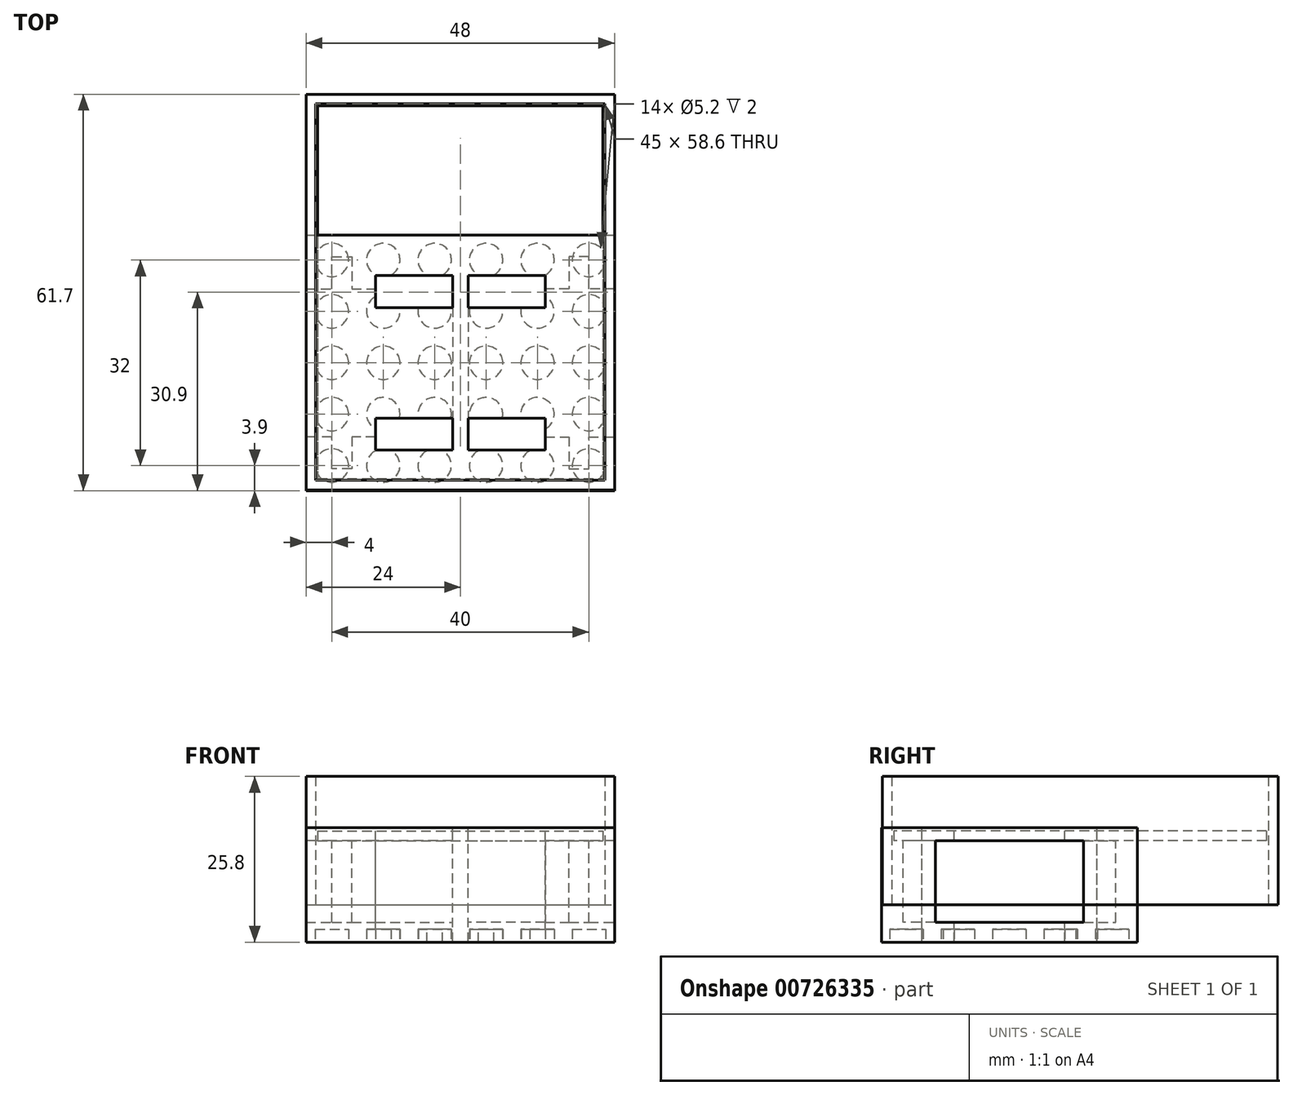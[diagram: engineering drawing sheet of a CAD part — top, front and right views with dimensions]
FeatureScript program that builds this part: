
annotation { "Feature Type Name" : "Feature", "Feature Type Description" : "" }
export const myFeature = defineFeature(function(context is Context, id is Id, definition is map)
    precondition{}
    {
        {
            var Q0;
            Q0=qCreatedBy(makeId("Top.planeOp"),FACE);
            var sketch = newSketch(context, id + "F0", { "sketchPlane" : qUnion([Q0])});
            skLineSegment(sketch, "E0.bottom", {"start": v(-24, 20) * mm, "end": v(24, 20) * mm});
            skLineSegment(sketch, "E0.top", {"start": v(-24, -20) * mm, "end": v(24, -20) * mm});
            skLineSegment(sketch, "E0.left", {"start": v(-24, 20) * mm, "end": v(-24, -20) * mm});
            skLineSegment(sketch, "E0.right", {"start": v(24, 20) * mm, "end": v(24, -20) * mm});
            skSolve(sketch);
        }
        {
            var Q0;
            Q0=makeQuery(id+"F0.imprint","IMPRINT",FACE,{"disambiguationData":[TD([[makeQuery(id+"F0.imprint","IMPRINT",EDGE,{"derivedFrom":sQuery(id+"F0.wireOp",EDGE,"E0.bottom")}),-1.0]])]});
            extrude(context, id + "F1", {"entities" : qUnion([Q0]), "depth" : 2 * mm, "offsetDistance" : 25 * mm});
        }
        {
            var Q0;
            Q0=qCreatedBy(makeId("Top.planeOp"),FACE);
            var sketch = newSketch(context, id + "F2", { "sketchPlane" : qUnion([Q0])});
            skLineSegment(sketch, "E1.bottom", {"start": v(24, -11.23) * mm, "end": v(19.7, -11.23) * mm});
            skLineSegment(sketch, "E1.top", {"start": v(24, 11.23) * mm, "end": v(19.7, 11.23) * mm});
            skLineSegment(sketch, "E1.left", {"start": v(24, -11.23) * mm, "end": v(24, 11.23) * mm});
            skLineSegment(sketch, "E1.right", {"start": v(1.5, -11.23) * mm, "end": v(1.5, 11.23) * mm});
            skLineSegment(sketch, "E2", {"start": v(19.7, -11.23) * mm, "end": v(19.7, -16.23) * mm});
            skLineSegment(sketch, "E3", {"start": v(19.7, -16.23) * mm, "end": v(17.2, -16.23) * mm});
            skLineSegment(sketch, "E4", {"start": v(17.2, -16.23) * mm, "end": v(17.2, -11.23) * mm});
            skLineSegment(sketch, "E5", {"start": v(19.7, 11.23) * mm, "end": v(19.7, 16.23) * mm});
            skLineSegment(sketch, "E6", {"start": v(19.7, 16.23) * mm, "end": v(17.2, 16.23) * mm});
            skLineSegment(sketch, "E7", {"start": v(17.2, 16.23) * mm, "end": v(17.2, 11.23) * mm});
            skLineSegment(sketch, "E8.trimOffspring", {"start": v(17.2, -11.23) * mm, "end": v(1.5, -11.23) * mm});
            skLineSegment(sketch, "E9.trimOffspring", {"start": v(17.2, 11.23) * mm, "end": v(1.5, 11.23) * mm});
            skLineSegment(sketch, "E10.MirrorCS", {"start": v(-24, -11.23) * mm, "end": v(-19.7, -11.23) * mm});
            skLineSegment(sketch, "E11.MirrorCS", {"start": v(-24, 11.23) * mm, "end": v(-19.7, 11.23) * mm});
            skLineSegment(sketch, "E12.MirrorCS", {"start": v(-24, -11.23) * mm, "end": v(-24, 11.23) * mm});
            skLineSegment(sketch, "E13.MirrorCS", {"start": v(-1.5, -11.23) * mm, "end": v(-1.5, 11.23) * mm});
            skLineSegment(sketch, "E14.MirrorCS", {"start": v(-19.7, -11.23) * mm, "end": v(-19.7, -16.23) * mm});
            skLineSegment(sketch, "E15.MirrorCS", {"start": v(-19.7, 16.23) * mm, "end": v(-17.2, 16.23) * mm});
            skLineSegment(sketch, "E16.MirrorCS", {"start": v(-19.7, -16.23) * mm, "end": v(-17.2, -16.23) * mm});
            skLineSegment(sketch, "E17.MirrorCS", {"start": v(-19.7, 11.23) * mm, "end": v(-19.7, 16.23) * mm});
            skLineSegment(sketch, "E18.MirrorCS", {"start": v(-17.2, -16.23) * mm, "end": v(-17.2, -11.23) * mm});
            skLineSegment(sketch, "E19.MirrorCS", {"start": v(-17.2, -11.23) * mm, "end": v(-1.5, -11.23) * mm});
            skLineSegment(sketch, "E20.MirrorCS", {"start": v(-17.2, 16.23) * mm, "end": v(-17.2, 11.23) * mm});
            skLineSegment(sketch, "E21.MirrorCS", {"start": v(-17.2, 11.23) * mm, "end": v(-1.5, 11.23) * mm});
            skSolve(sketch);
        }
        {
            var Q0;
            Q0=makeQuery(id+"F1.opExtrude","CAP_FACE",FACE,{"disambiguationData":[OSD([sQuery(id+"F0.wireOp",EDGE,"E0.bottom"),sQuery(id+"F0.wireOp",EDGE,"E0.top"),sQuery(id+"F0.wireOp",EDGE,"E0.left"),sQuery(id+"F0.wireOp",EDGE,"E0.right")])],"isStart":true});
            var sketch = newSketch(context, id + "F3", { "sketchPlane" : qUnion([Q0])});
            skLineSegment(sketch, "E22.bottom", {"start": v(24, -27.9) * mm, "end": v(-1, -27.9) * mm});
            skLineSegment(sketch, "E22.top", {"start": v(24, 27.9) * mm, "end": v(-1, 27.9) * mm});
            skLineSegment(sketch, "E22.left", {"start": v(24, -27.9) * mm, "end": v(24, -11.53) * mm});
            skLineSegment(sketch, "E22.right", {"start": v(-1, -27.9) * mm, "end": v(-1, 27.9) * mm});
            skLineSegment(sketch, "E23", {"start": v(24, -11.53) * mm, "end": v(20, -11.53) * mm});
            skLineSegment(sketch, "E24", {"start": v(20, -11.53) * mm, "end": v(20, -16.53) * mm});
            skLineSegment(sketch, "E25", {"start": v(20, -16.53) * mm, "end": v(16.9, -16.53) * mm});
            skLineSegment(sketch, "E26", {"start": v(16.9, -16.53) * mm, "end": v(16.9, -11.53) * mm});
            skLineSegment(sketch, "E27", {"start": v(16.9, -11.53) * mm, "end": v(1.2, -11.53) * mm});
            skLineSegment(sketch, "E28", {"start": v(1.2, -11.53) * mm, "end": v(1.2, 11.53) * mm});
            skLineSegment(sketch, "E29", {"start": v(1.2, 11.53) * mm, "end": v(16.9, 11.53) * mm});
            skLineSegment(sketch, "E30", {"start": v(16.9, 11.53) * mm, "end": v(16.9, 16.53) * mm});
            skLineSegment(sketch, "E31", {"start": v(16.9, 16.53) * mm, "end": v(20, 16.53) * mm});
            skLineSegment(sketch, "E32", {"start": v(20, 16.53) * mm, "end": v(20, 11.53) * mm});
            skLineSegment(sketch, "E33", {"start": v(20, 11.53) * mm, "end": v(24, 11.53) * mm});
            skLineSegment(sketch, "E34.trimOffspring", {"start": v(24, 11.53) * mm, "end": v(24, 27.9) * mm});
            skLineSegment(sketch, "E35.MirrorCS", {"start": v(-16.9, 16.53) * mm, "end": v(-20, 16.53) * mm});
            skLineSegment(sketch, "E36.MirrorCS", {"start": v(-16.9, 11.53) * mm, "end": v(-16.9, 16.53) * mm});
            skLineSegment(sketch, "E37.MirrorCS", {"start": v(-1.2, 11.53) * mm, "end": v(-16.9, 11.53) * mm});
            skLineSegment(sketch, "E38.MirrorCS", {"start": v(-1.2, -11.53) * mm, "end": v(-1.2, 11.53) * mm});
            skLineSegment(sketch, "E39.MirrorCS", {"start": v(-16.9, -11.53) * mm, "end": v(-1.2, -11.53) * mm});
            skLineSegment(sketch, "E40.MirrorCS", {"start": v(-16.9, -16.53) * mm, "end": v(-16.9, -11.53) * mm});
            skLineSegment(sketch, "E41.MirrorCS", {"start": v(-20, -16.53) * mm, "end": v(-16.9, -16.53) * mm});
            skLineSegment(sketch, "E42.MirrorCS", {"start": v(-20, -11.53) * mm, "end": v(-20, -16.53) * mm});
            skLineSegment(sketch, "E43.MirrorCS", {"start": v(-24, -11.53) * mm, "end": v(-20, -11.53) * mm});
            skLineSegment(sketch, "E44.MirrorCS", {"start": v(1, -27.9) * mm, "end": v(1, 27.9) * mm});
            skLineSegment(sketch, "E45.MirrorCS", {"start": v(-24, -27.9) * mm, "end": v(-24, -11.53) * mm});
            skLineSegment(sketch, "E46.MirrorCS", {"start": v(-24, 27.9) * mm, "end": v(1, 27.9) * mm});
            skLineSegment(sketch, "E47.MirrorCS", {"start": v(-24, -27.9) * mm, "end": v(1, -27.9) * mm});
            skLineSegment(sketch, "E48.MirrorCS", {"start": v(-24, 11.53) * mm, "end": v(-24, 27.9) * mm});
            skLineSegment(sketch, "E49.MirrorCS", {"start": v(-20, 16.53) * mm, "end": v(-20, 11.53) * mm});
            skLineSegment(sketch, "E50.MirrorCS", {"start": v(-20, 11.53) * mm, "end": v(-24, 11.53) * mm});
            skSolve(sketch);
        }
        {
            var Q0;
            Q0 = qSketchRegion(id + "F3", true);
            extrude(context, id + "F4", {"entities" : qUnion([Q0]), "depth" : 12.7 * mm, "offsetDistance" : 25 * mm});
        }
        {
            var Q0;
            Q0=makeQuery(id+"F4.opExtrude","CAP_FACE",FACE,{"disambiguationData":[OSD([sQuery(id+"F3.wireOp",EDGE,"E22.bottom"),sQuery(id+"F3.wireOp",EDGE,"E22.top"),sQuery(id+"F3.wireOp",EDGE,"E22.left"),sQuery(id+"F3.wireOp",EDGE,"E22.right"),sQuery(id+"F3.wireOp",EDGE,"E23"),sQuery(id+"F3.wireOp",EDGE,"E24"),sQuery(id+"F3.wireOp",EDGE,"E25"),sQuery(id+"F3.wireOp",EDGE,"E26"),sQuery(id+"F3.wireOp",EDGE,"E27"),sQuery(id+"F3.wireOp",EDGE,"E28"),sQuery(id+"F3.wireOp",EDGE,"E29"),sQuery(id+"F3.wireOp",EDGE,"E30"),sQuery(id+"F3.wireOp",EDGE,"E31"),sQuery(id+"F3.wireOp",EDGE,"E32"),sQuery(id+"F3.wireOp",EDGE,"E33"),sQuery(id+"F3.wireOp",EDGE,"E34.trimOffspring")])],"isStart":false});
            var sketch = newSketch(context, id + "F5", { "sketchPlane" : qUnion([Q0])});
            skLineSegment(sketch, "E51.bottom", {"start": v(24, -27.9) * mm, "end": v(-24, -27.9) * mm});
            skLineSegment(sketch, "E51.top", {"start": v(24, 27.9) * mm, "end": v(-24, 27.9) * mm});
            skLineSegment(sketch, "E51.left", {"start": v(24, -27.9) * mm, "end": v(24, 27.9) * mm});
            skLineSegment(sketch, "E51.right", {"start": v(-24, -27.9) * mm, "end": v(-24, 27.9) * mm});
            skSolve(sketch);
        }
        {
            var Q0;
            Q0 = qSketchRegion(id + "F5", true);
            extrude(context, id + "F6", {"entities" : qUnion([Q0]), "operationType" : NewBodyOperationType.ADD, "depth" : 3.1 * mm, "offsetDistance" : 25 * mm});
        }
        {
            var Q0;
            Q0=makeQuery(id+"F4.opExtrude","CAP_FACE",FACE,{"disambiguationData":[OSD([sQuery(id+"F3.wireOp",EDGE,"E22.bottom"),sQuery(id+"F3.wireOp",EDGE,"E22.top"),sQuery(id+"F3.wireOp",EDGE,"E22.left"),sQuery(id+"F3.wireOp",EDGE,"E22.right"),sQuery(id+"F3.wireOp",EDGE,"E23"),sQuery(id+"F3.wireOp",EDGE,"E24"),sQuery(id+"F3.wireOp",EDGE,"E25"),sQuery(id+"F3.wireOp",EDGE,"E26"),sQuery(id+"F3.wireOp",EDGE,"E27"),sQuery(id+"F3.wireOp",EDGE,"E28"),sQuery(id+"F3.wireOp",EDGE,"E29"),sQuery(id+"F3.wireOp",EDGE,"E30"),sQuery(id+"F3.wireOp",EDGE,"E31"),sQuery(id+"F3.wireOp",EDGE,"E32"),sQuery(id+"F3.wireOp",EDGE,"E33"),sQuery(id+"F3.wireOp",EDGE,"E34.trimOffspring")])],"isStart":true});
            var sketch = newSketch(context, id + "F7", { "sketchPlane" : qUnion([Q0])});
            skLineSegment(sketch, "E52", {"start": v(42.9, 0) * mm, "end": v(-13.7, 0) * mm, "construction": true});
            skCircle(sketch, "E53", {"center": v(4, -16) * mm, "radius": 2.4 * mm});
            skCircle(sketch, "E54", {"center": v(12, -16) * mm, "radius": 2.4 * mm});
            skCircle(sketch, "E55", {"center": v(4, -24) * mm, "radius": 2.4 * mm});
            skCircle(sketch, "E56", {"center": v(12, -24) * mm, "radius": 2.4 * mm});
            skCircle(sketch, "E57", {"center": v(20, -24) * mm, "radius": 2.4 * mm});
            skCircle(sketch, "E58.MirrorC", {"center": v(20, 24) * mm, "radius": 2.4 * mm});
            skCircle(sketch, "E59.MirrorC", {"center": v(12, 16) * mm, "radius": 2.4 * mm});
            skCircle(sketch, "E60.MirrorC", {"center": v(4, 16) * mm, "radius": 2.4 * mm});
            skCircle(sketch, "E61.MirrorC", {"center": v(12, 24) * mm, "radius": 2.4 * mm});
            skCircle(sketch, "E62.MirrorC", {"center": v(4, 24) * mm, "radius": 2.4 * mm});
            skCircle(sketch, "E63.MirrorC", {"center": v(-20, -24) * mm, "radius": 2.4 * mm});
            skCircle(sketch, "E64.MirrorC", {"center": v(-4, 16) * mm, "radius": 2.4 * mm});
            skCircle(sketch, "E65.MirrorC", {"center": v(-12, 16) * mm, "radius": 2.4 * mm});
            skCircle(sketch, "E66.MirrorC", {"center": v(-12, -24) * mm, "radius": 2.4 * mm});
            skCircle(sketch, "E67.MirrorC", {"center": v(-4, -16) * mm, "radius": 2.4 * mm});
            skCircle(sketch, "E68.MirrorC", {"center": v(-4, -24) * mm, "radius": 2.4 * mm});
            skCircle(sketch, "E69.MirrorC", {"center": v(-12, -16) * mm, "radius": 2.4 * mm});
            skCircle(sketch, "E70.MirrorC", {"center": v(-20, 24) * mm, "radius": 2.4 * mm});
            skCircle(sketch, "E71.MirrorC", {"center": v(-4, 24) * mm, "radius": 2.4 * mm});
            skCircle(sketch, "E72.MirrorC", {"center": v(-12, 24) * mm, "radius": 2.4 * mm});
            skSolve(sketch);
        }
        {
            var Q0;
            Q0 = qSketchRegion(id + "F7", true);
            extrude(context, id + "F8", {"entities" : qUnion([Q0]), "operationType" : NewBodyOperationType.ADD, "depth" : 1.6 * mm, "offsetDistance" : 25 * mm});
        }
        {
            var Q0;
            {var subQ0=sQuery(id+"F5.wireOp",EDGE,"E51.left");Q0=makeQuery(id+"F6.boolean.opBoolean","SPLIT",FACE,{"disambiguationData":[TD([makeQuery(id+"F4.opExtrude","SWEPT_FACE",FACE,{"disambiguationData":[OSD([sQuery(id+"F3.wireOp",EDGE,"E22.left")])]})])],"derivedFrom":makeQuery(id+"F6.opExtrude","CAP_FACE",FACE,{"disambiguationData":[OSD([sQuery(id+"F5.wireOp",EDGE,"E51.bottom"),sQuery(id+"F5.wireOp",EDGE,"E51.top"),subQ0,sQuery(id+"F5.wireOp",EDGE,"E51.right")])],"isStart":true})});}
            var sketch = newSketch(context, id + "F9", { "sketchPlane" : qUnion([Q0])});
            skLineSegment(sketch, "E73.bottom", {"start": v(1.2, -8.6) * mm, "end": v(13.2, -8.6) * mm});
            skLineSegment(sketch, "E73.top", {"start": v(1.2, -13.6) * mm, "end": v(13.2, -13.6) * mm});
            skLineSegment(sketch, "E73.left", {"start": v(1.2, -8.6) * mm, "end": v(1.2, -13.6) * mm});
            skLineSegment(sketch, "E73.right", {"start": v(13.2, -8.6) * mm, "end": v(13.2, -13.6) * mm});
            skLineSegment(sketch, "E74.MirrorCS", {"start": v(-1.2, -8.6) * mm, "end": v(-13.2, -8.6) * mm});
            skLineSegment(sketch, "E75.MirrorCS", {"start": v(-13.2, -8.6) * mm, "end": v(-13.2, -13.6) * mm});
            skLineSegment(sketch, "E76.MirrorCS", {"start": v(-1.2, -8.6) * mm, "end": v(-1.2, -13.6) * mm});
            skLineSegment(sketch, "E77.MirrorCS", {"start": v(-1.2, -13.6) * mm, "end": v(-13.2, -13.6) * mm});
            skLineSegment(sketch, "E78.MirrorCS", {"start": v(-1.2, 8.6) * mm, "end": v(-1.2, 13.6) * mm});
            skLineSegment(sketch, "E79.MirrorCS", {"start": v(1.2, 8.6) * mm, "end": v(13.2, 8.6) * mm});
            skLineSegment(sketch, "E80.MirrorCS", {"start": v(13.2, 8.6) * mm, "end": v(13.2, 13.6) * mm});
            skLineSegment(sketch, "E81.MirrorCS", {"start": v(-1.2, 13.6) * mm, "end": v(-13.2, 13.6) * mm});
            skLineSegment(sketch, "E82.MirrorCS", {"start": v(-13.2, 8.6) * mm, "end": v(-13.2, 13.6) * mm});
            skLineSegment(sketch, "E83.MirrorCS", {"start": v(-1.2, 8.6) * mm, "end": v(-13.2, 8.6) * mm});
            skLineSegment(sketch, "E84.MirrorCS", {"start": v(1.2, 8.6) * mm, "end": v(1.2, 13.6) * mm});
            skLineSegment(sketch, "E85.MirrorCS", {"start": v(1.2, 13.6) * mm, "end": v(13.2, 13.6) * mm});
            skSolve(sketch);
        }
        {
            var Q0;
            Q0 = qSketchRegion(id + "F9", true);
            extrude(context, id + "F10", {"entities" : qUnion([Q0]), "operationType" : NewBodyOperationType.REMOVE, "endBound" : BoundingType.SYMMETRIC, "oppositeDirection" : true, "depth" : 50 * mm, "offsetDistance" : 25 * mm});
        }
        {
            var Q0;
            Q0=makeQuery(id+"F4.opExtrude","CAP_FACE",FACE,{"disambiguationData":[OSD([sQuery(id+"F3.wireOp",EDGE,"E22.bottom"),sQuery(id+"F3.wireOp",EDGE,"E22.top"),sQuery(id+"F3.wireOp",EDGE,"E22.left"),sQuery(id+"F3.wireOp",EDGE,"E23"),sQuery(id+"F3.wireOp",EDGE,"E24"),sQuery(id+"F3.wireOp",EDGE,"E25"),sQuery(id+"F3.wireOp",EDGE,"E26"),sQuery(id+"F3.wireOp",EDGE,"E27"),sQuery(id+"F3.wireOp",EDGE,"E28"),sQuery(id+"F3.wireOp",EDGE,"E29"),sQuery(id+"F3.wireOp",EDGE,"E30"),sQuery(id+"F3.wireOp",EDGE,"E31"),sQuery(id+"F3.wireOp",EDGE,"E32"),sQuery(id+"F3.wireOp",EDGE,"E33"),sQuery(id+"F3.wireOp",EDGE,"E34.trimOffspring"),sQuery(id+"F3.wireOp",EDGE,"E35.MirrorCS"),sQuery(id+"F3.wireOp",EDGE,"E36.MirrorCS"),sQuery(id+"F3.wireOp",EDGE,"E37.MirrorCS"),sQuery(id+"F3.wireOp",EDGE,"E38.MirrorCS"),sQuery(id+"F3.wireOp",EDGE,"E39.MirrorCS"),sQuery(id+"F3.wireOp",EDGE,"E40.MirrorCS"),sQuery(id+"F3.wireOp",EDGE,"E41.MirrorCS"),sQuery(id+"F3.wireOp",EDGE,"E42.MirrorCS"),sQuery(id+"F3.wireOp",EDGE,"E43.MirrorCS"),sQuery(id+"F3.wireOp",EDGE,"E45.MirrorCS"),sQuery(id+"F3.wireOp",EDGE,"E46.MirrorCS"),sQuery(id+"F3.wireOp",EDGE,"E47.MirrorCS"),sQuery(id+"F3.wireOp",EDGE,"E48.MirrorCS"),sQuery(id+"F3.wireOp",EDGE,"E49.MirrorCS"),sQuery(id+"F3.wireOp",EDGE,"E50.MirrorCS")])],"isStart":true});
            var sketch = newSketch(context, id + "F11", { "sketchPlane" : qUnion([Q0])});
            skLineSegment(sketch, "E86.bottom", {"start": v(-32.74, 19.9) * mm, "end": v(43.37, 19.9) * mm});
            skLineSegment(sketch, "E86.top", {"start": v(-32.74, 44.05) * mm, "end": v(43.37, 44.05) * mm});
            skLineSegment(sketch, "E86.left", {"start": v(-32.74, 19.9) * mm, "end": v(-32.74, 44.05) * mm});
            skLineSegment(sketch, "E86.right", {"start": v(43.37, 19.9) * mm, "end": v(43.37, 44.05) * mm});
            skLineSegment(sketch, "E87.bottom", {"start": v(-31.38, -34.8) * mm, "end": v(34.1, -34.8) * mm});
            skLineSegment(sketch, "E87.top", {"start": v(-31.38, -19.9) * mm, "end": v(34.1, -19.9) * mm});
            skLineSegment(sketch, "E87.left", {"start": v(-31.38, -34.8) * mm, "end": v(-31.38, -19.9) * mm});
            skLineSegment(sketch, "E87.right", {"start": v(34.1, -34.8) * mm, "end": v(34.1, -19.9) * mm});
            skSolve(sketch);
        }
        {
            var Q0;
            Q0 = qSketchRegion(id + "F11", true);
            extrude(context, id + "F12", {"entities" : qUnion([Q0]), "operationType" : NewBodyOperationType.REMOVE, "endBound" : BoundingType.SYMMETRIC, "oppositeDirection" : true, "depth" : 50 * mm, "offsetDistance" : 25 * mm});
        }
        {
            var Q0;
            Q0=makeQuery(id+"F6.opExtrude","CAP_FACE",FACE,{"disambiguationData":[OSD([sQuery(id+"F5.wireOp",EDGE,"E51.bottom"),sQuery(id+"F5.wireOp",EDGE,"E51.top"),sQuery(id+"F5.wireOp",EDGE,"E51.left"),sQuery(id+"F5.wireOp",EDGE,"E51.right")])],"isStart":false});
            var sketch = newSketch(context, id + "F13", { "sketchPlane" : qUnion([Q0])});
            skCircle(sketch, "E88", {"center": v(4, 8) * mm, "radius": 2.6 * mm});
            skCircle(sketch, "E89", {"center": v(12, 8) * mm, "radius": 2.6 * mm});
            skCircle(sketch, "E90", {"center": v(20, 8) * mm, "radius": 2.6 * mm});
            skCircle(sketch, "E91", {"center": v(20, 16) * mm, "radius": 2.6 * mm});
            skCircle(sketch, "E92", {"center": v(12, 16) * mm, "radius": 2.6 * mm});
            skCircle(sketch, "E93", {"center": v(4, 16) * mm, "radius": 2.6 * mm});
            skCircle(sketch, "E94.MirrorC", {"center": v(4, -8) * mm, "radius": 2.6 * mm});
            skCircle(sketch, "E95.MirrorC", {"center": v(12, -8) * mm, "radius": 2.6 * mm});
            skCircle(sketch, "E96.MirrorC", {"center": v(12, -16) * mm, "radius": 2.6 * mm});
            skCircle(sketch, "E97.MirrorC", {"center": v(4, -16) * mm, "radius": 2.6 * mm});
            skCircle(sketch, "E98.MirrorC", {"center": v(20, -8) * mm, "radius": 2.6 * mm});
            skCircle(sketch, "E99.MirrorC", {"center": v(20, -16) * mm, "radius": 2.6 * mm});
            skCircle(sketch, "E100", {"center": v(20, 0) * mm, "radius": 2.6 * mm});
            skCircle(sketch, "E101", {"center": v(12, 0) * mm, "radius": 2.6 * mm});
            skCircle(sketch, "E102", {"center": v(4, 0) * mm, "radius": 2.6 * mm});
            skCircle(sketch, "E103.MirrorC", {"center": v(-12, 8) * mm, "radius": 2.6 * mm});
            skCircle(sketch, "E104.MirrorC", {"center": v(-20, 8) * mm, "radius": 2.6 * mm});
            skCircle(sketch, "E105.MirrorC", {"center": v(-4, 8) * mm, "radius": 2.6 * mm});
            skCircle(sketch, "E106.MirrorC", {"center": v(-20, 0) * mm, "radius": 2.6 * mm});
            skCircle(sketch, "E107.MirrorC", {"center": v(-20, -8) * mm, "radius": 2.6 * mm});
            skCircle(sketch, "E108.MirrorC", {"center": v(-4, -16) * mm, "radius": 2.6 * mm});
            skCircle(sketch, "E109.MirrorC", {"center": v(-12, -16) * mm, "radius": 2.6 * mm});
            skCircle(sketch, "E110.MirrorC", {"center": v(-4, 0) * mm, "radius": 2.6 * mm});
            skCircle(sketch, "E111.MirrorC", {"center": v(-12, -8) * mm, "radius": 2.6 * mm});
            skCircle(sketch, "E112.MirrorC", {"center": v(-12, 0) * mm, "radius": 2.6 * mm});
            skCircle(sketch, "E113.MirrorC", {"center": v(-20, 16) * mm, "radius": 2.6 * mm});
            skCircle(sketch, "E114.MirrorC", {"center": v(-20, -16) * mm, "radius": 2.6 * mm});
            skCircle(sketch, "E115.MirrorC", {"center": v(-4, -8) * mm, "radius": 2.6 * mm});
            skCircle(sketch, "E116.MirrorC", {"center": v(-4, 16) * mm, "radius": 2.6 * mm});
            skCircle(sketch, "E117.MirrorC", {"center": v(-12, 16) * mm, "radius": 2.6 * mm});
            skSolve(sketch);
        }
        {
            var Q0;
            Q0 = qSketchRegion(id + "F13", true);
            extrude(context, id + "F14", {"entities" : qUnion([Q0]), "operationType" : NewBodyOperationType.REMOVE, "oppositeDirection" : true, "depth" : 2 * mm, "offsetDistance" : 25 * mm});
        }
        {
            var Q0;
            Q0=makeQuery(id+"F6.opExtrude","CAP_FACE",FACE,{"disambiguationData":[OSD([sQuery(id+"F5.wireOp",EDGE,"E51.bottom"),sQuery(id+"F5.wireOp",EDGE,"E51.top"),sQuery(id+"F5.wireOp",EDGE,"E51.left"),sQuery(id+"F5.wireOp",EDGE,"E51.right")])],"isStart":false});
            var sketch = newSketch(context, id + "F15", { "sketchPlane" : qUnion([Q0])});
            skLineSegment(sketch, "E118.bottom", {"start": v(13.2, 12.62) * mm, "end": v(10.8, 12.62) * mm});
            skLineSegment(sketch, "E118.top", {"start": v(13.2, 15.52) * mm, "end": v(10.8, 15.52) * mm});
            skLineSegment(sketch, "E118.left", {"start": v(13.2, 12.62) * mm, "end": v(13.2, 15.52) * mm});
            skLineSegment(sketch, "E118.right", {"start": v(10.8, 12.62) * mm, "end": v(10.8, 15.52) * mm});
            skLineSegment(sketch, "E119", {"start": v(12, 16) * mm, "end": v(12, 11.4) * mm, "construction": true});
            skLineSegment(sketch, "E120", {"start": v(4, 16) * mm, "end": v(4, 11.42) * mm, "construction": true});
            skLineSegment(sketch, "E121.bottom", {"start": v(5.2, 15.52) * mm, "end": v(2.8, 15.52) * mm});
            skLineSegment(sketch, "E121.top", {"start": v(5.2, 12.4) * mm, "end": v(2.8, 12.4) * mm});
            skLineSegment(sketch, "E121.left", {"start": v(5.2, 15.52) * mm, "end": v(5.2, 12.4) * mm});
            skLineSegment(sketch, "E121.right", {"start": v(2.8, 15.52) * mm, "end": v(2.8, 12.4) * mm});
            skLineSegment(sketch, "E122.MirrorCS", {"start": v(5.2, -15.52) * mm, "end": v(2.8, -15.52) * mm});
            skLineSegment(sketch, "E123.MirrorCS", {"start": v(13.2, -12.62) * mm, "end": v(10.8, -12.62) * mm});
            skLineSegment(sketch, "E124.MirrorCS", {"start": v(13.2, -15.52) * mm, "end": v(10.8, -15.52) * mm});
            skLineSegment(sketch, "E125.MirrorCS", {"start": v(13.2, -12.62) * mm, "end": v(13.2, -15.52) * mm});
            skLineSegment(sketch, "E126.MirrorCS", {"start": v(10.8, -12.62) * mm, "end": v(10.8, -15.52) * mm});
            skLineSegment(sketch, "E127.MirrorCS", {"start": v(5.2, -12.4) * mm, "end": v(2.8, -12.4) * mm});
            skLineSegment(sketch, "E128.MirrorCS", {"start": v(2.8, -15.52) * mm, "end": v(2.8, -12.4) * mm});
            skLineSegment(sketch, "E129.MirrorCS", {"start": v(5.2, -15.52) * mm, "end": v(5.2, -12.4) * mm});
            skLineSegment(sketch, "E130.MirrorCS", {"start": v(-5.2, 15.52) * mm, "end": v(-2.8, 15.52) * mm});
            skLineSegment(sketch, "E131.MirrorCS", {"start": v(-5.2, 12.4) * mm, "end": v(-2.8, 12.4) * mm});
            skLineSegment(sketch, "E132.MirrorCS", {"start": v(-13.2, 15.52) * mm, "end": v(-10.8, 15.52) * mm});
            skLineSegment(sketch, "E133.MirrorCS", {"start": v(-5.2, 15.52) * mm, "end": v(-5.2, 12.4) * mm});
            skLineSegment(sketch, "E134.MirrorCS", {"start": v(-5.2, -15.52) * mm, "end": v(-2.8, -15.52) * mm});
            skLineSegment(sketch, "E135.MirrorCS", {"start": v(-13.2, -12.62) * mm, "end": v(-13.2, -15.52) * mm});
            skLineSegment(sketch, "E136.MirrorCS", {"start": v(-13.2, 12.62) * mm, "end": v(-13.2, 15.52) * mm});
            skLineSegment(sketch, "E137.MirrorCS", {"start": v(-13.2, -12.62) * mm, "end": v(-10.8, -12.62) * mm});
            skLineSegment(sketch, "E138.MirrorCS", {"start": v(-2.8, 15.52) * mm, "end": v(-2.8, 12.4) * mm});
            skLineSegment(sketch, "E139.MirrorCS", {"start": v(-13.2, -15.52) * mm, "end": v(-10.8, -15.52) * mm});
            skLineSegment(sketch, "E140.MirrorCS", {"start": v(-10.8, 12.62) * mm, "end": v(-10.8, 15.52) * mm});
            skLineSegment(sketch, "E141.MirrorCS", {"start": v(-13.2, 12.62) * mm, "end": v(-10.8, 12.62) * mm});
            skLineSegment(sketch, "E142.MirrorCS", {"start": v(-5.2, -12.4) * mm, "end": v(-2.8, -12.4) * mm});
            skLineSegment(sketch, "E143.MirrorCS", {"start": v(-10.8, -12.62) * mm, "end": v(-10.8, -15.52) * mm});
            skLineSegment(sketch, "E144.MirrorCS", {"start": v(-5.2, -15.52) * mm, "end": v(-5.2, -12.4) * mm});
            skLineSegment(sketch, "E145.MirrorCS", {"start": v(-2.8, -15.52) * mm, "end": v(-2.8, -12.4) * mm});
            skSolve(sketch);
        }
        {
            var Q0;
            Q0 = qSketchRegion(id + "F15", true);
            var Q1;
            Q1=makeQuery(id+"F14.boolean.opBoolean","COPY",FACE,{"derivedFrom":makeQuery(id+"F14.opExtrude","CAP_FACE",FACE,{"disambiguationData":[OSD([sQuery(id+"F13.wireOp",EDGE,"E92")])],"isStart":false})});
            extrude(context, id + "F16", {"entities" : qUnion([Q0]), "operationType" : NewBodyOperationType.REMOVE, "endBound" : BoundingType.UP_TO_SURFACE, "oppositeDirection" : true, "depth" : 25 * mm, "endBoundEntityFace" : qUnion([Q1]), "offsetDistance" : 25 * mm});
        }
        {
            var Q0;
            Q0=qCreatedBy(makeId("Top.planeOp"),FACE);
            var sketch = newSketch(context, id + "F17", { "sketchPlane" : qUnion([Q0])});
            skLineSegment(sketch, "E146.bottom", {"start": v(-22.2, 40) * mm, "end": v(22.2, 40) * mm});
            skLineSegment(sketch, "E146.top", {"start": v(-22.2, -18) * mm, "end": v(22.2, -18) * mm});
            skLineSegment(sketch, "E146.left", {"start": v(-22.2, 40) * mm, "end": v(-22.2, -18) * mm});
            skLineSegment(sketch, "E146.right", {"start": v(22.2, 40) * mm, "end": v(22.2, -18) * mm});
            skLineSegment(sketch, "E147.bottom", {"start": v(6, 36.7) * mm, "end": v(11.9, 36.7) * mm});
            skLineSegment(sketch, "E147.top", {"start": v(6, 26.5) * mm, "end": v(11.9, 26.5) * mm});
            skLineSegment(sketch, "E147.left", {"start": v(6, 36.7) * mm, "end": v(6, 26.5) * mm});
            skLineSegment(sketch, "E147.right", {"start": v(11.9, 36.7) * mm, "end": v(11.9, 26.5) * mm});
            skLineSegment(sketch, "E148.MirrorCS", {"start": v(-6, 26.5) * mm, "end": v(-11.9, 26.5) * mm});
            skLineSegment(sketch, "E149.MirrorCS", {"start": v(-11.9, 36.7) * mm, "end": v(-11.9, 26.5) * mm});
            skLineSegment(sketch, "E150.MirrorCS", {"start": v(-6, 36.7) * mm, "end": v(-6, 26.5) * mm});
            skLineSegment(sketch, "E151.MirrorCS", {"start": v(-6, 36.7) * mm, "end": v(-11.9, 36.7) * mm});
            skSolve(sketch);
        }
        {
            var Q0;
            Q0=qCreatedBy(makeId("Top.planeOp"),FACE);
            var sketch = newSketch(context, id + "F18", { "sketchPlane" : qUnion([Q0])});
            skLineSegment(sketch, "E152.bottom", {"start": v(-22.5, 40.3) * mm, "end": v(22.5, 40.3) * mm});
            skLineSegment(sketch, "E152.top", {"start": v(-22.5, -18.3) * mm, "end": v(22.5, -18.3) * mm});
            skLineSegment(sketch, "E152.left", {"start": v(-22.5, 40.3) * mm, "end": v(-22.5, -18.3) * mm});
            skLineSegment(sketch, "E152.right", {"start": v(22.5, 40.3) * mm, "end": v(22.5, -18.3) * mm});
            skLineSegment(sketch, "E153.bottom", {"start": v(-24, 41.8) * mm, "end": v(24, 41.8) * mm});
            skLineSegment(sketch, "E153.top", {"start": v(-24, -19.8) * mm, "end": v(24, -19.8) * mm});
            skLineSegment(sketch, "E153.left", {"start": v(-24, 41.8) * mm, "end": v(-24, -19.8) * mm});
            skLineSegment(sketch, "E153.right", {"start": v(24, 41.8) * mm, "end": v(24, -19.8) * mm});
            skSolve(sketch);
        }
        {
            var Q0;
            Q0 = qSketchRegion(id + "F18", true);
            extrude(context, id + "F19", {"entities" : qUnion([Q0]), "depth" : 10 * mm, "offsetDistance" : 25 * mm, "hasSecondDirection" : true, "secondDirectionOppositeDirection" : true, "secondDirectionDepth" : 10 * mm});
        }
        {
            var Q0;
            Q0=qCreatedBy(makeId("Top.planeOp"),FACE);
            var sketch = newSketch(context, id + "F20", { "sketchPlane" : qUnion([Q0])});
            skLineSegment(sketch, "E154.bottom", {"start": v(-22.2, 40) * mm, "end": v(22.2, 40) * mm});
            skLineSegment(sketch, "E154.top", {"start": v(-22.2, -18) * mm, "end": v(22.2, -18) * mm});
            skLineSegment(sketch, "E154.left", {"start": v(-22.2, 40) * mm, "end": v(-22.2, -18) * mm});
            skLineSegment(sketch, "E154.right", {"start": v(22.2, 40) * mm, "end": v(22.2, -18) * mm});
            skSolve(sketch);
        }
        {
            var Q0;
            Q0 = qSketchRegion(id + "F20", true);
            extrude(context, id + "F21", {"entities" : qUnion([Q0]), "depth" : 1.5 * mm, "offsetDistance" : 25 * mm});
        }
    });
